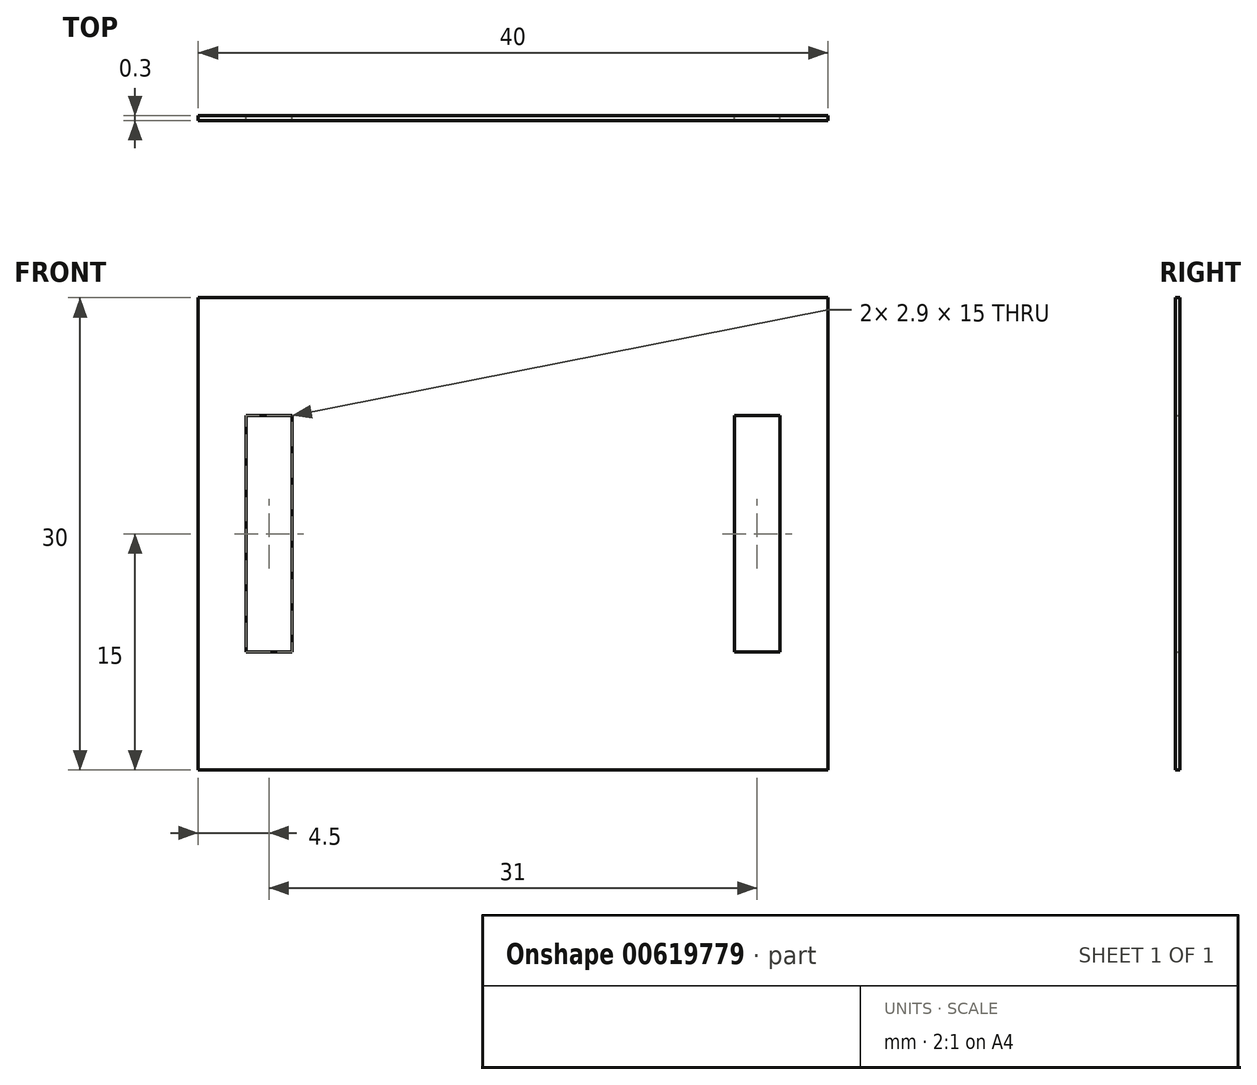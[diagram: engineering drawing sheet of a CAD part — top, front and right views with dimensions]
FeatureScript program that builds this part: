
annotation { "Feature Type Name" : "Feature", "Feature Type Description" : "" }
export const myFeature = defineFeature(function(context is Context, id is Id, definition is map)
    precondition{}
    {
        {
            var Q0;
            Q0=qCreatedBy(makeId("Front.planeOp"),FACE);
            var sketch = newSketch(context, id + "F0", { "sketchPlane" : qUnion([Q0])});
            skLineSegment(sketch, "E0.bottom", {"start": v(-17, 7.5) * mm, "end": v(-14, 7.5) * mm, "construction": true});
            skLineSegment(sketch, "E0.top", {"start": v(-17, -7.5) * mm, "end": v(-14, -7.5) * mm, "construction": true});
            skLineSegment(sketch, "E0.left", {"start": v(-17, 7.5) * mm, "end": v(-17, -7.5) * mm, "construction": true});
            skLineSegment(sketch, "E0.right", {"start": v(-14, 7.5) * mm, "end": v(-14, -7.5) * mm, "construction": true});
            skLineSegment(sketch, "E1", {"start": v(-20, 0) * mm, "end": v(20, 0) * mm, "construction": true});
            skLineSegment(sketch, "E2", {"start": v(0, -15) * mm, "end": v(0, 15) * mm, "construction": true});
            skLineSegment(sketch, "E3.MirrorCS", {"start": v(17, 7.5) * mm, "end": v(14, 7.5) * mm, "construction": true});
            skLineSegment(sketch, "E4.MirrorCS", {"start": v(14, 7.5) * mm, "end": v(14, -7.5) * mm, "construction": true});
            skLineSegment(sketch, "E5.MirrorCS", {"start": v(17, 7.5) * mm, "end": v(17, -7.5) * mm, "construction": true});
            skLineSegment(sketch, "E6.MirrorCS", {"start": v(17, -7.5) * mm, "end": v(14, -7.5) * mm, "construction": true});
            skLineSegment(sketch, "E7.bottom", {"start": v(20, 15) * mm, "end": v(-20, 15) * mm});
            skLineSegment(sketch, "E7.top", {"start": v(20, -15) * mm, "end": v(-20, -15) * mm});
            skLineSegment(sketch, "E7.left", {"start": v(20, 15) * mm, "end": v(20, -15) * mm});
            skLineSegment(sketch, "E7.right", {"start": v(-20, 15) * mm, "end": v(-20, -15) * mm});
            skLineSegment(sketch, "E8.bottom", {"start": v(16.95, 7.5) * mm, "end": v(14.05, 7.5) * mm});
            skLineSegment(sketch, "E8.top", {"start": v(16.95, -7.5) * mm, "end": v(14.05, -7.5) * mm});
            skLineSegment(sketch, "E8.left", {"start": v(16.95, 7.5) * mm, "end": v(16.95, -7.5) * mm});
            skLineSegment(sketch, "E8.right", {"start": v(14.05, 7.5) * mm, "end": v(14.05, -7.5) * mm});
            skLineSegment(sketch, "E9.MirrorCS", {"start": v(-16.95, -7.5) * mm, "end": v(-14.05, -7.5) * mm});
            skLineSegment(sketch, "E10.MirrorCS", {"start": v(-14.05, 7.5) * mm, "end": v(-14.05, -7.5) * mm});
            skLineSegment(sketch, "E11.MirrorCS", {"start": v(-16.95, 7.5) * mm, "end": v(-14.05, 7.5) * mm});
            skLineSegment(sketch, "E12.MirrorCS", {"start": v(-16.95, 7.5) * mm, "end": v(-16.95, -7.5) * mm});
            skSolve(sketch);
        }
        {
            var Q0;
            Q0 = qSketchRegion(id + "F0", true);
            extrude(context, id + "F1", {"entities" : qUnion([Q0]), "depth" : 0.3 * mm, "offsetDistance" : 25 * mm});
        }
    });
